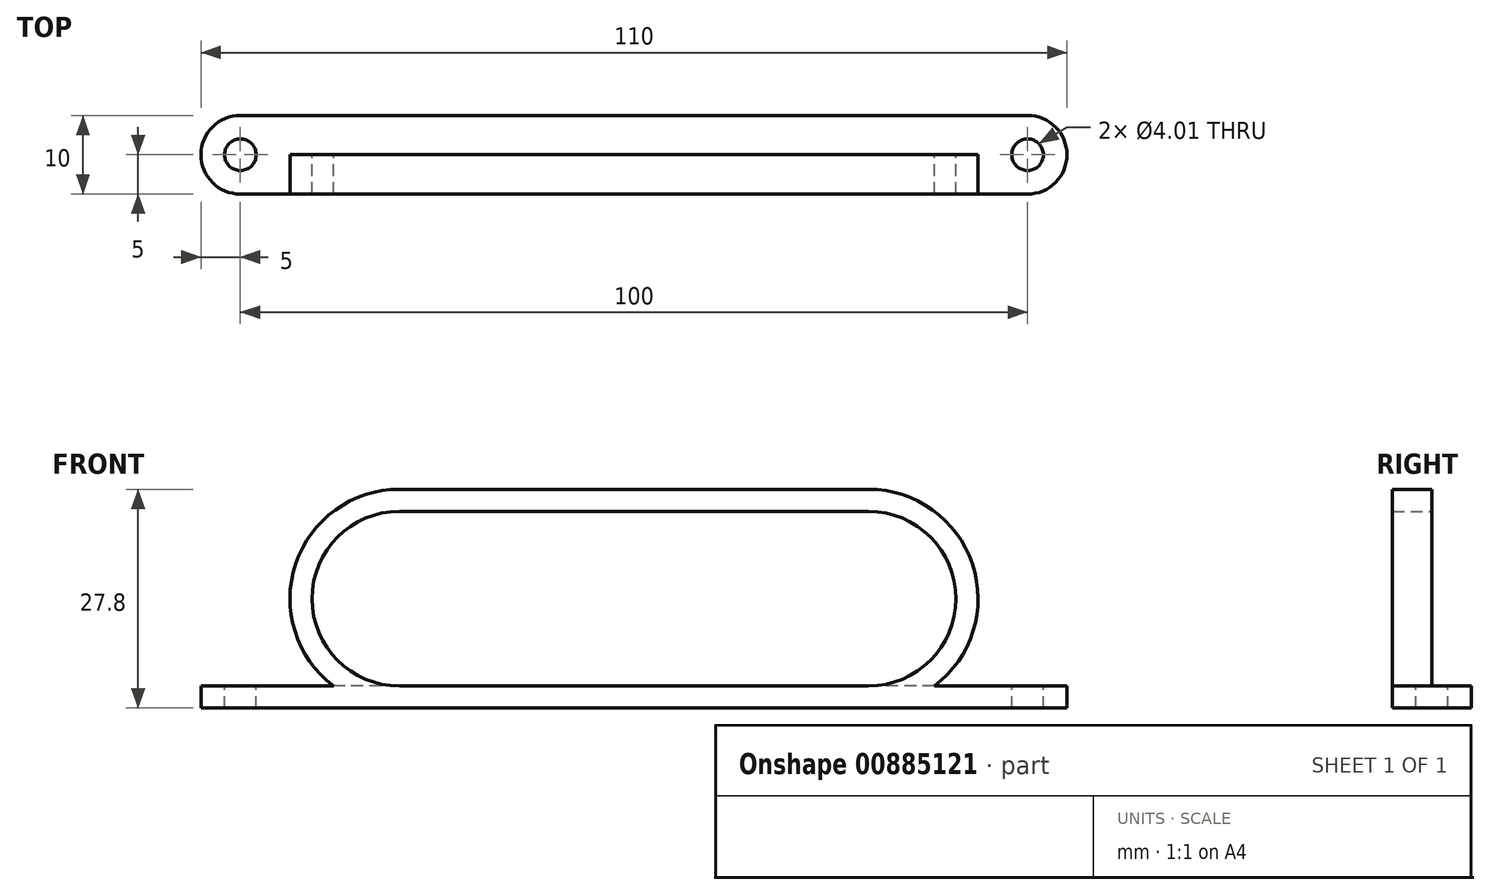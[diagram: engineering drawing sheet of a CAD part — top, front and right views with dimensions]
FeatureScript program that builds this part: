
annotation { "Feature Type Name" : "Feature", "Feature Type Description" : "" }
export const myFeature = defineFeature(function(context is Context, id is Id, definition is map)
    precondition{}
    {
        {
            var Q0;
            Q0=qCreatedBy(makeId("Front.planeOp"),FACE);
            var sketch = newSketch(context, id + "F0", { "sketchPlane" : qUnion([Q0])});
            skLineSegment(sketch, "E0.bottom", {"start": v(29.8, -11.1) * mm, "end": v(-29.8, -11.1) * mm});
            skLineSegment(sketch, "E0.top", {"start": v(29.8, 11.1) * mm, "end": v(-29.8, 11.1) * mm});
            skPoint(sketch, "E0.middle", {"position": v(0, 0) * mm});
            skArc(sketch, "E1", {"start": v(-29.8, 11.1) * mm, "mid": v(-40.9, 0) * mm, "end": v(-29.8, -11.1) * mm});
            skArc(sketch, "E2", {"start": v(29.8, -11.1) * mm, "mid": v(40.9, 0) * mm, "end": v(29.8, 11.1) * mm});
            skLineSegment(sketch, "E3.0", {"start": v(29.8, -13.9) * mm, "end": v(-29.8, -13.9) * mm});
            skArc(sketch, "E3.1", {"start": v(29.8, -13.9) * mm, "mid": v(43.7, 0) * mm, "end": v(29.8, 13.9) * mm});
            skArc(sketch, "E3.3", {"start": v(-29.8, 13.9) * mm, "mid": v(-43.7, 0) * mm, "end": v(-29.8, -13.9) * mm});
            skLineSegment(sketch, "E4", {"start": v(-29.8, 13.9) * mm, "end": v(29.8, 13.9) * mm});
            skPoint(sketch, "E5", {"position": v(0, 18.7) * mm});
            skSolve(sketch);
        }
        {
            var Q0;
            Q0 = qSketchRegion(id + "F0", true);
            extrude(context, id + "F1", {"entities" : qUnion([Q0]), "depth" : 5 * mm, "offsetDistance" : 25 * mm});
        }
        {
            var Q0;
            Q0=makeQuery(id+"F1.opExtrude","CAP_FACE",FACE,{"disambiguationData":[OSD([sQuery(id+"F0.wireOp",EDGE,"E0.bottom"),sQuery(id+"F0.wireOp",EDGE,"E0.top"),sQuery(id+"F0.wireOp",EDGE,"E1"),sQuery(id+"F0.wireOp",EDGE,"E2"),sQuery(id+"F0.wireOp",EDGE,"E3.0"),sQuery(id+"F0.wireOp",EDGE,"E3.1"),sQuery(id+"F0.wireOp",EDGE,"E3.3"),sQuery(id+"F0.wireOp",EDGE,"E4")])],"isStart":false});
            var sketch = newSketch(context, id + "F2", { "sketchPlane" : qUnion([Q0])});
            skLineSegment(sketch, "E6.bottom", {"start": v(60, -13.9) * mm, "end": v(-60, -13.9) * mm});
            skLineSegment(sketch, "E6.top", {"start": v(60, -11.1) * mm, "end": v(-60, -11.1) * mm});
            skLineSegment(sketch, "E6.left", {"start": v(60, -13.9) * mm, "end": v(60, -11.1) * mm});
            skLineSegment(sketch, "E6.right", {"start": v(-60, -13.9) * mm, "end": v(-60, -11.1) * mm});
            skPoint(sketch, "E6.middle", {"position": v(0, -12.5) * mm});
            skSolve(sketch);
        }
        {
            var Q0;
            Q0 = qSketchRegion(id + "F2", true);
            extrude(context, id + "F3", {"entities" : qUnion([Q0]), "operationType" : NewBodyOperationType.ADD, "oppositeDirection" : true, "depth" : 10 * mm, "offsetDistance" : 25 * mm});
        }
        {
            var Q0;
            Q0=makeQuery(id+"F3.boolean.opBoolean","MERGE",FACE,{"derivedFrom":[makeQuery(id+"F1.opExtrude","SWEPT_FACE",FACE,{"disambiguationData":[OSD([sQuery(id+"F0.wireOp",EDGE,"E0.bottom")])]}),makeQuery(id+"F3.opExtrude","SWEPT_FACE",FACE,{"disambiguationData":[OSD([sQuery(id+"F2.wireOp",EDGE,"E6.top")])]})]});
            var sketch = newSketch(context, id + "F4", { "sketchPlane" : qUnion([Q0])});
            skCircle(sketch, "E7", {"center": v(50, 0) * mm, "radius": 2 * mm});
            skLineSegment(sketch, "E8", {"start": v(0, 0) * mm, "end": v(0, 30.53) * mm, "construction": true});
            skCircle(sketch, "E9.MirrorC", {"center": v(-50, 0) * mm, "radius": 2 * mm});
            skSolve(sketch);
        }
        {
            var Q0;
            Q0 = qSketchRegion(id + "F4", true);
            extrude(context, id + "F5", {"entities" : qUnion([Q0]), "operationType" : NewBodyOperationType.REMOVE, "endBound" : BoundingType.THROUGH_ALL, "oppositeDirection" : true, "depth" : 25 * mm, "offsetDistance" : 25 * mm});
        }
        {
            var Q0;
            Q0=makeQuery(id+"F3.boolean.opBoolean","MERGE",FACE,{"derivedFrom":[makeQuery(id+"F1.opExtrude","SWEPT_FACE",FACE,{"disambiguationData":[OSD([sQuery(id+"F0.wireOp",EDGE,"E0.bottom")])]}),makeQuery(id+"F3.opExtrude","SWEPT_FACE",FACE,{"disambiguationData":[OSD([sQuery(id+"F2.wireOp",EDGE,"E6.top")])]})]});
            var sketch = newSketch(context, id + "F6", { "sketchPlane" : qUnion([Q0])});
            skArc(sketch, "E10", {"start": v(-50, 5) * mm, "mid": v(-55, 0) * mm, "end": v(-50, -5) * mm});
            skLineSegment(sketch, "E11.bottom", {"start": v(-50, 5) * mm, "end": v(-60, 5) * mm});
            skLineSegment(sketch, "E11.top", {"start": v(-50, -5) * mm, "end": v(-60, -5) * mm});
            skLineSegment(sketch, "E11.right", {"start": v(-60, 5) * mm, "end": v(-60, -5) * mm});
            skLineSegment(sketch, "E12.MirrorCS", {"start": v(50, 5) * mm, "end": v(60, 5) * mm});
            skLineSegment(sketch, "E13.MirrorCS", {"start": v(60, 5) * mm, "end": v(60, -5) * mm});
            skLineSegment(sketch, "E14.MirrorCS", {"start": v(50, -5) * mm, "end": v(60, -5) * mm});
            skArc(sketch, "E15.MirrorCS", {"start": v(50, 5) * mm, "mid": v(55, 0) * mm, "end": v(50, -5) * mm});
            skSolve(sketch);
        }
        {
            var Q0;
            Q0 = qSketchRegion(id + "F6", true);
            extrude(context, id + "F7", {"entities" : qUnion([Q0]), "operationType" : NewBodyOperationType.REMOVE, "endBound" : BoundingType.THROUGH_ALL, "oppositeDirection" : true, "depth" : 25 * mm, "offsetDistance" : 25 * mm});
        }
    });
